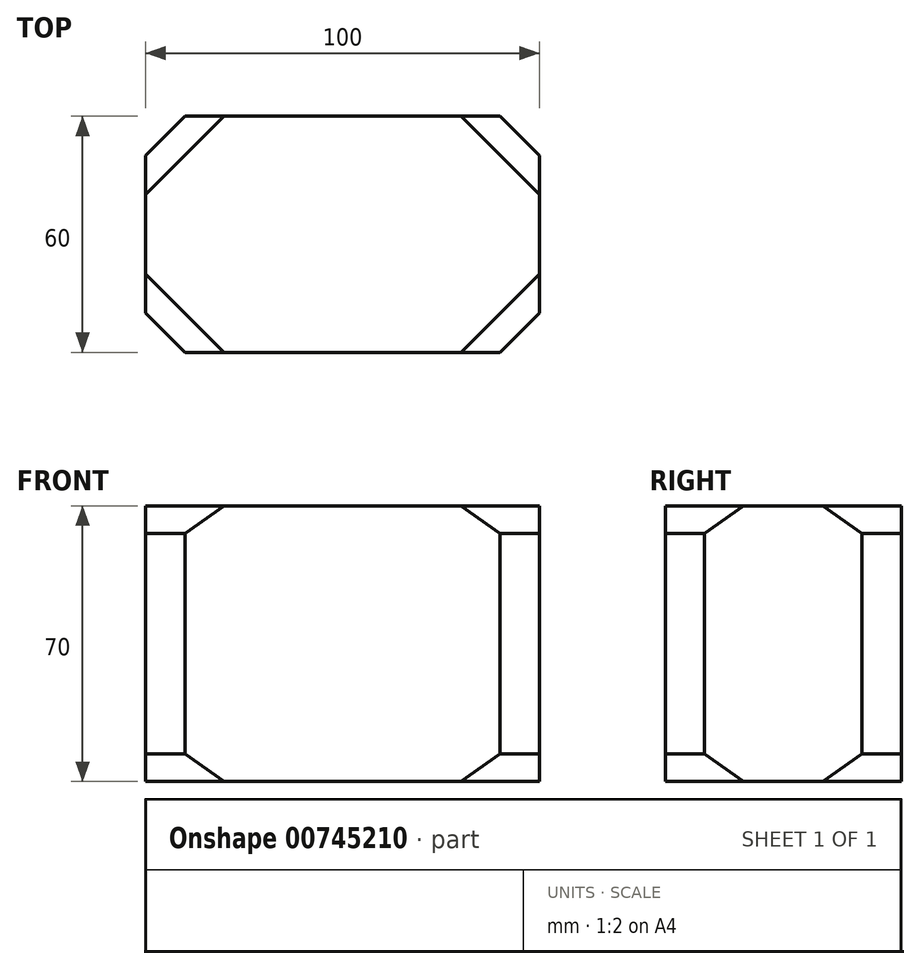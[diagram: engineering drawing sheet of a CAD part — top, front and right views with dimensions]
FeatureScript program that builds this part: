
annotation { "Feature Type Name" : "Feature", "Feature Type Description" : "" }
export const myFeature = defineFeature(function(context is Context, id is Id, definition is map)
    precondition{}
    {
        {
            var Q0;
            Q0=qCreatedBy(makeId("Top.planeOp"),FACE);
            var sketch = newSketch(context, id + "F0", { "sketchPlane" : qUnion([Q0])});
            skLineSegment(sketch, "E0.bottom", {"start": v(-50, -30) * mm, "end": v(50, -30) * mm});
            skLineSegment(sketch, "E0.top", {"start": v(-50, 30) * mm, "end": v(50, 30) * mm});
            skLineSegment(sketch, "E0.left", {"start": v(-50, -30) * mm, "end": v(-50, 30) * mm});
            skLineSegment(sketch, "E0.right", {"start": v(50, -30) * mm, "end": v(50, 30) * mm});
            skPoint(sketch, "E0.middle", {"position": v(0, 0) * mm});
            skSolve(sketch);
        }
        {
            var Q0;
            Q0 = qSketchRegion(id + "F0", true);
            extrude(context, id + "F1", {"entities" : qUnion([Q0]), "depth" : 70 * mm, "offsetDistance" : 25 * mm});
        }
        {
            var Q0;
            Q0=makeQuery(id+"F1.opExtrude","SWEPT_EDGE",EDGE,{"disambiguationData":[OSD([sQuery(id+"F0.wireOp",EDGE,"E0.bottom"),sQuery(id+"F0.wireOp",EDGE,"E0.left")])]});
            var Q1;
            Q1=makeQuery(id+"F1.opExtrude","SWEPT_EDGE",EDGE,{"disambiguationData":[OSD([sQuery(id+"F0.wireOp",EDGE,"E0.bottom"),sQuery(id+"F0.wireOp",EDGE,"E0.right")])]});
            var Q2;
            Q2=makeQuery(id+"F1.opExtrude","SWEPT_EDGE",EDGE,{"disambiguationData":[OSD([sQuery(id+"F0.wireOp",EDGE,"E0.top"),sQuery(id+"F0.wireOp",EDGE,"E0.right")])]});
            var Q3;
            Q3=makeQuery(id+"F1.opExtrude","SWEPT_EDGE",EDGE,{"disambiguationData":[OSD([sQuery(id+"F0.wireOp",EDGE,"E0.top"),sQuery(id+"F0.wireOp",EDGE,"E0.left")])]});
            chamfer(context, id + "F2", {"entities" : qUnion([Q0, Q1, Q2, Q3]), "width" : 10 * mm, "tangentPropagation" : true});
        }
        {
            var Q0;
            {var subQ0=sQuery(id+"F0.wireOp",EDGE,"E0.right");var subQ1=sQuery(id+"F0.wireOp",EDGE,"E0.top");Q0=makeQuery(id+"F2.opChamfer","BLEND_EDGE",EDGE,{"blendedFrom":[makeQuery(id+"F1.opExtrude","SWEPT_EDGE",EDGE,{"disambiguationData":[OSD([subQ1,subQ0])]}),makeQuery(id+"F1.opExtrude","CAP_FACE",FACE,{"disambiguationData":[OSD([sQuery(id+"F0.wireOp",EDGE,"E0.bottom"),subQ1,sQuery(id+"F0.wireOp",EDGE,"E0.left"),subQ0])],"isStart":false})],"blendedInto":[makeQuery(id+"F1.opExtrude","CAP_FACE",FACE,{"disambiguationData":[OSD([sQuery(id+"F0.wireOp",EDGE,"E0.bottom"),subQ1,sQuery(id+"F0.wireOp",EDGE,"E0.left"),subQ0])],"isStart":false})]});}
            var Q1;
            {var subQ0=sQuery(id+"F0.wireOp",EDGE,"E0.right");var subQ1=sQuery(id+"F0.wireOp",EDGE,"E0.top");Q1=makeQuery(id+"F2.opChamfer","BLEND_EDGE",EDGE,{"blendedFrom":[makeQuery(id+"F1.opExtrude","SWEPT_EDGE",EDGE,{"disambiguationData":[OSD([subQ1,subQ0])]}),makeQuery(id+"F1.opExtrude","CAP_FACE",FACE,{"disambiguationData":[OSD([sQuery(id+"F0.wireOp",EDGE,"E0.bottom"),subQ1,sQuery(id+"F0.wireOp",EDGE,"E0.left"),subQ0])],"isStart":true})],"blendedInto":[makeQuery(id+"F1.opExtrude","CAP_FACE",FACE,{"disambiguationData":[OSD([sQuery(id+"F0.wireOp",EDGE,"E0.bottom"),subQ1,sQuery(id+"F0.wireOp",EDGE,"E0.left"),subQ0])],"isStart":true})]});}
            var Q2;
            {var subQ0=sQuery(id+"F0.wireOp",EDGE,"E0.left");var subQ1=sQuery(id+"F0.wireOp",EDGE,"E0.top");Q2=makeQuery(id+"F2.opChamfer","BLEND_EDGE",EDGE,{"blendedFrom":[makeQuery(id+"F1.opExtrude","SWEPT_EDGE",EDGE,{"disambiguationData":[OSD([subQ1,subQ0])]}),makeQuery(id+"F1.opExtrude","CAP_FACE",FACE,{"disambiguationData":[OSD([sQuery(id+"F0.wireOp",EDGE,"E0.bottom"),subQ1,subQ0,sQuery(id+"F0.wireOp",EDGE,"E0.right")])],"isStart":false})],"blendedInto":[makeQuery(id+"F1.opExtrude","CAP_FACE",FACE,{"disambiguationData":[OSD([sQuery(id+"F0.wireOp",EDGE,"E0.bottom"),subQ1,subQ0,sQuery(id+"F0.wireOp",EDGE,"E0.right")])],"isStart":false})]});}
            var Q3;
            {var subQ0=sQuery(id+"F0.wireOp",EDGE,"E0.left");var subQ1=sQuery(id+"F0.wireOp",EDGE,"E0.top");Q3=makeQuery(id+"F2.opChamfer","BLEND_EDGE",EDGE,{"blendedFrom":[makeQuery(id+"F1.opExtrude","SWEPT_EDGE",EDGE,{"disambiguationData":[OSD([subQ1,subQ0])]}),makeQuery(id+"F1.opExtrude","CAP_FACE",FACE,{"disambiguationData":[OSD([sQuery(id+"F0.wireOp",EDGE,"E0.bottom"),subQ1,subQ0,sQuery(id+"F0.wireOp",EDGE,"E0.right")])],"isStart":true})],"blendedInto":[makeQuery(id+"F1.opExtrude","CAP_FACE",FACE,{"disambiguationData":[OSD([sQuery(id+"F0.wireOp",EDGE,"E0.bottom"),subQ1,subQ0,sQuery(id+"F0.wireOp",EDGE,"E0.right")])],"isStart":true})]});}
            var Q4;
            {var subQ0=sQuery(id+"F0.wireOp",EDGE,"E0.left");var subQ1=sQuery(id+"F0.wireOp",EDGE,"E0.bottom");Q4=makeQuery(id+"F2.opChamfer","BLEND_EDGE",EDGE,{"blendedFrom":[makeQuery(id+"F1.opExtrude","SWEPT_EDGE",EDGE,{"disambiguationData":[OSD([subQ1,subQ0])]}),makeQuery(id+"F1.opExtrude","CAP_FACE",FACE,{"disambiguationData":[OSD([subQ1,sQuery(id+"F0.wireOp",EDGE,"E0.top"),subQ0,sQuery(id+"F0.wireOp",EDGE,"E0.right")])],"isStart":false})],"blendedInto":[makeQuery(id+"F1.opExtrude","CAP_FACE",FACE,{"disambiguationData":[OSD([subQ1,sQuery(id+"F0.wireOp",EDGE,"E0.top"),subQ0,sQuery(id+"F0.wireOp",EDGE,"E0.right")])],"isStart":false})]});}
            var Q5;
            {var subQ0=sQuery(id+"F0.wireOp",EDGE,"E0.right");var subQ1=sQuery(id+"F0.wireOp",EDGE,"E0.bottom");Q5=makeQuery(id+"F2.opChamfer","BLEND_EDGE",EDGE,{"blendedFrom":[makeQuery(id+"F1.opExtrude","SWEPT_EDGE",EDGE,{"disambiguationData":[OSD([subQ1,subQ0])]}),makeQuery(id+"F1.opExtrude","CAP_FACE",FACE,{"disambiguationData":[OSD([subQ1,sQuery(id+"F0.wireOp",EDGE,"E0.top"),sQuery(id+"F0.wireOp",EDGE,"E0.left"),subQ0])],"isStart":false})],"blendedInto":[makeQuery(id+"F1.opExtrude","CAP_FACE",FACE,{"disambiguationData":[OSD([subQ1,sQuery(id+"F0.wireOp",EDGE,"E0.top"),sQuery(id+"F0.wireOp",EDGE,"E0.left"),subQ0])],"isStart":false})]});}
            var Q6;
            {var subQ0=sQuery(id+"F0.wireOp",EDGE,"E0.left");var subQ1=sQuery(id+"F0.wireOp",EDGE,"E0.bottom");Q6=makeQuery(id+"F2.opChamfer","BLEND_EDGE",EDGE,{"blendedFrom":[makeQuery(id+"F1.opExtrude","SWEPT_EDGE",EDGE,{"disambiguationData":[OSD([subQ1,subQ0])]}),makeQuery(id+"F1.opExtrude","CAP_FACE",FACE,{"disambiguationData":[OSD([subQ1,sQuery(id+"F0.wireOp",EDGE,"E0.top"),subQ0,sQuery(id+"F0.wireOp",EDGE,"E0.right")])],"isStart":true})],"blendedInto":[makeQuery(id+"F1.opExtrude","CAP_FACE",FACE,{"disambiguationData":[OSD([subQ1,sQuery(id+"F0.wireOp",EDGE,"E0.top"),subQ0,sQuery(id+"F0.wireOp",EDGE,"E0.right")])],"isStart":true})]});}
            var Q7;
            {var subQ0=sQuery(id+"F0.wireOp",EDGE,"E0.right");var subQ1=sQuery(id+"F0.wireOp",EDGE,"E0.bottom");Q7=makeQuery(id+"F2.opChamfer","BLEND_EDGE",EDGE,{"blendedFrom":[makeQuery(id+"F1.opExtrude","SWEPT_EDGE",EDGE,{"disambiguationData":[OSD([subQ1,subQ0])]}),makeQuery(id+"F1.opExtrude","CAP_FACE",FACE,{"disambiguationData":[OSD([subQ1,sQuery(id+"F0.wireOp",EDGE,"E0.top"),sQuery(id+"F0.wireOp",EDGE,"E0.left"),subQ0])],"isStart":true})],"blendedInto":[makeQuery(id+"F1.opExtrude","CAP_FACE",FACE,{"disambiguationData":[OSD([subQ1,sQuery(id+"F0.wireOp",EDGE,"E0.top"),sQuery(id+"F0.wireOp",EDGE,"E0.left"),subQ0])],"isStart":true})]});}
            chamfer(context, id + "F3", {"entities" : qUnion([Q0, Q1, Q2, Q3, Q4, Q5, Q6, Q7]), "width" : 7 * mm, "tangentPropagation" : true});
        }
    });
